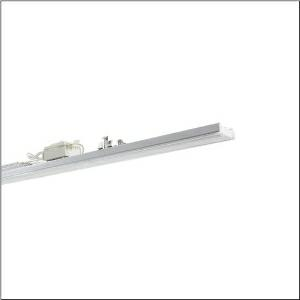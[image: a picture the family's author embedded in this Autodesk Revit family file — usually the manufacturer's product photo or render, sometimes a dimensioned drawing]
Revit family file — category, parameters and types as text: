
# Revit family: licross_r__11_recessed_mo_51te14dn49xg_c518
name_source: partatom
category: Lighting Fixtures
units: mm (PartAtom-declared; Revit-internal decimal feet)

## family parameters
Cut with Voids When Loaded = No
Host = Face
Light Source = No
Part Type = Normal
Room Calculation Point = No
Round Connector Dimension = Use Diameter
Shared = No

## types (1)
- --- (1 x LED, 9430 lm, 56.7 W, 4000K)
    Apparent Load = 57 VA
    CIE Flux Codes = 56 84 97 100 100
    Color Rendering = 80
    Color Temperature = 4000K
    Default Elevation = 1800 mm
    Description = Licross® 11 Recessed MO, luminaire insert, of sheet steel, galvanised, coil coated, white, length: 1.500mm, width: 66mm, height: 67mm, LED rated luminous flux: 9.430lm, light colour: 840, control gear: DALI 2, with plug, 5-pole, with phase selection, mains connection: 220..240V, AC, 50/60Hz, rated input power: 57W, internal wiring halogen-free, primary light control with lens, of plastic, primary optical cover: cover, of PMMA, light emission: direct distribution, primary light characteristic: asymmetric, protection rating (complete): IP54, insulation class (complete): insulation class I (protective earthing), certification: CE, ENEC, VDE, UKCA, protection symbol: D if used in an environment with non-conductive dust loads with corresponding accessories, impact resistance: IK06, permissible ambient temperature for indoor applications: -25..+35°C, corresponds to IFS (International Featured Standards) requirements for safety and quality in the food industry, reducing of maximum allowable ambient temperature of 5°C with ceiling mounting, LABS conformity tested according to VDMA 24364:2018-05, packaging unit: 1 piece
    Height = 58 mm
    Lamp = 1 x LED
    Lamp Light Flux = 9430 lm
    Lamp Power = 56.7 W
    Lamp count = 1
    Length = 1500 mm
    Luminous efficacy = 166 lm/W
    Manufacturer = Siteco
    ModVariant = No
    Model = 51TE14DN49XG
    Mounting Place = Ceiling
    Mounting Type = Pendant
    Number of Poles = 1
    OnlyDefault = Yes
    Power Factor = 1
    Product Name = Licross® 11 Recessed MO
    Product group = luminaire insert | ceiling pendant
    ProductGroupID = 902
    Protection Class = Protection class I
    Protection Degree = IP 54
    RLX_Detail_Level = 1
    RLX_Emergency_Light_Flux = 0 lm
    RLX_Emergency_Type = 0
    RLX_Emergency_Type_DB = No
    RlxData = <blob elided: 25005 chars, md5=8fea33ac>
    Socket = socket
    Standby Power = 0 W
    System Light Flux = 9430 lm
    System Power = 57 W
    Type Comments = factory setting: luminous flux: 100 % | dim-lin: 254 | 378 mA
    Type Image = l_1296930.jpg
    URL = http://relux.com
    VarID = @adj_121455
    Voltage = 0 V
    Weight = 0.00 kg
    Width = 66 mm

## geometry (parser evidence)
native form markers: Blend x4, Sweep x11
no freeform markers — native parametric forms only
